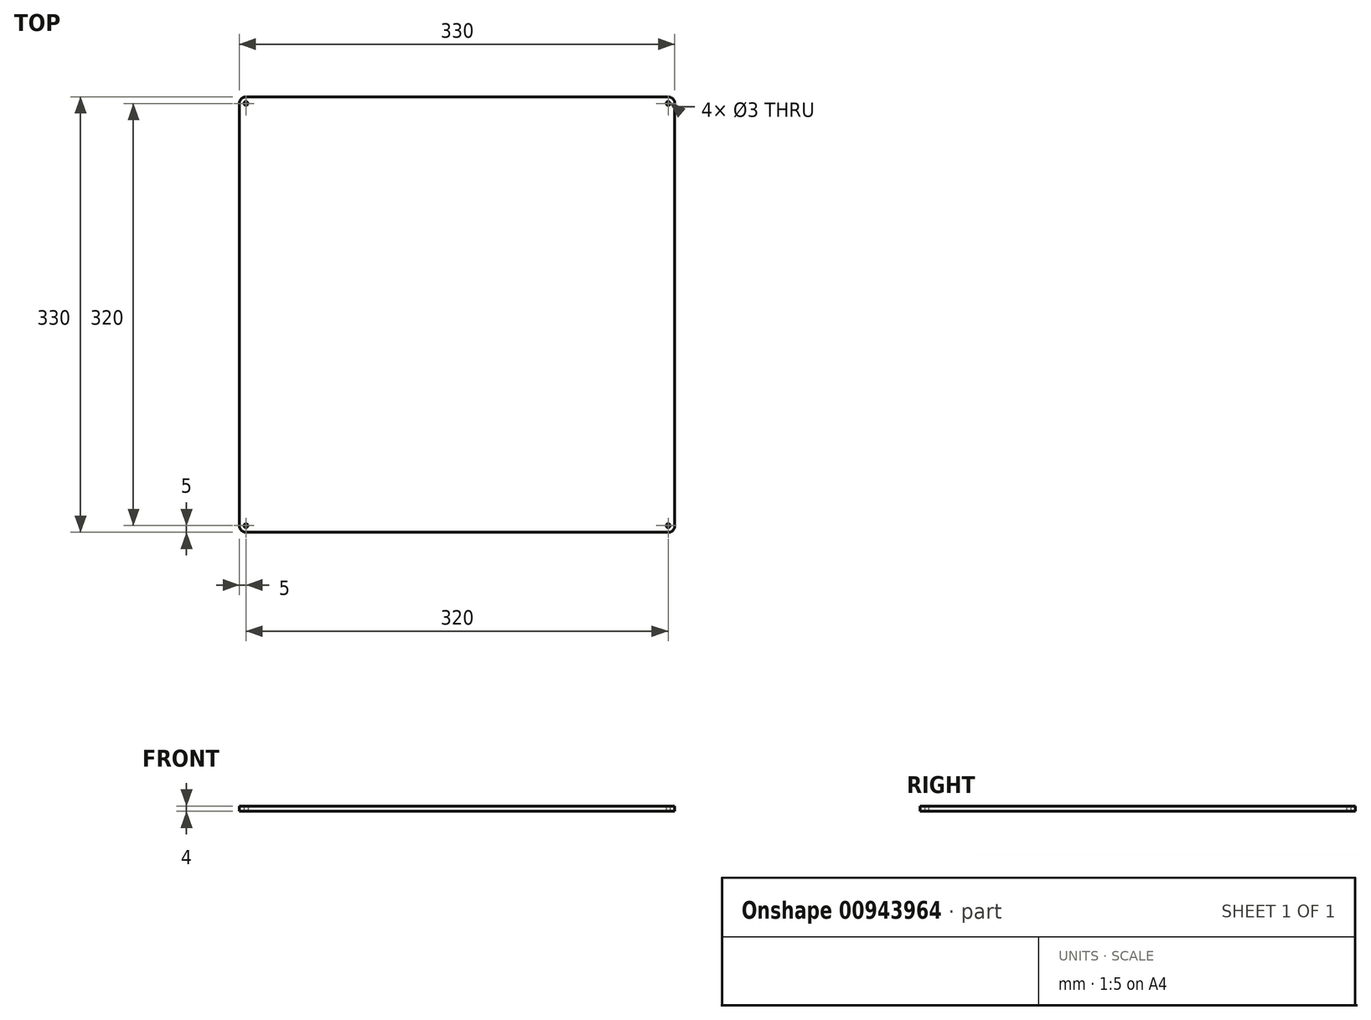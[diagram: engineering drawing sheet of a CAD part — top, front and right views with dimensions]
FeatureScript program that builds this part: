
annotation { "Feature Type Name" : "Feature", "Feature Type Description" : "" }
export const myFeature = defineFeature(function(context is Context, id is Id, definition is map)
    precondition{}
    {
        {
            var Q0;
            Q0=qCreatedBy(makeId("Top.planeOp"),FACE);
            var sketch = newSketch(context, id + "F0", { "sketchPlane" : qUnion([Q0])});
            skLineSegment(sketch, "E0.bottom", {"start": v(165, -165) * mm, "end": v(-165, -165) * mm});
            skLineSegment(sketch, "E0.top", {"start": v(165, 165) * mm, "end": v(-165, 165) * mm});
            skLineSegment(sketch, "E0.left", {"start": v(165, -165) * mm, "end": v(165, 165) * mm});
            skLineSegment(sketch, "E0.right", {"start": v(-165, -165) * mm, "end": v(-165, 165) * mm});
            skPoint(sketch, "E0.middle", {"position": v(0, 0) * mm});
            skCircle(sketch, "E1", {"center": v(-160, 160) * mm, "radius": 1.5 * mm});
            skCircle(sketch, "E2", {"center": v(160, 160) * mm, "radius": 1.5 * mm});
            skCircle(sketch, "E3", {"center": v(160, -160) * mm, "radius": 1.5 * mm});
            skCircle(sketch, "E4", {"center": v(-160, -160) * mm, "radius": 1.5 * mm});
            skSolve(sketch);
        }
        {
            var Q0;
            Q0=makeQuery(id+"F0.imprint","IMPRINT",FACE,{"disambiguationData":[TD([[makeQuery(id+"F0.imprint","IMPRINT",EDGE,{"derivedFrom":sQuery(id+"F0.wireOp",EDGE,"E0.bottom")}),-1.0]])]});
            extrude(context, id + "F1", {"entities" : qUnion([Q0]), "depth" : 4 * mm, "offsetDistance" : 25 * mm});
        }
        {
            var Q0;
            Q0=makeQuery(id+"F1.opExtrude","SWEPT_EDGE",EDGE,{"disambiguationData":[OSD([sQuery(id+"F0.wireOp",EDGE,"E0.bottom"),sQuery(id+"F0.wireOp",EDGE,"E0.left")])]});
            var Q1;
            Q1=makeQuery(id+"F1.opExtrude","SWEPT_EDGE",EDGE,{"disambiguationData":[OSD([sQuery(id+"F0.wireOp",EDGE,"E0.bottom"),sQuery(id+"F0.wireOp",EDGE,"E0.right")])]});
            var Q2;
            Q2=makeQuery(id+"F1.opExtrude","SWEPT_EDGE",EDGE,{"disambiguationData":[OSD([sQuery(id+"F0.wireOp",EDGE,"E0.top"),sQuery(id+"F0.wireOp",EDGE,"E0.right")])]});
            var Q3;
            Q3=makeQuery(id+"F1.opExtrude","SWEPT_EDGE",EDGE,{"disambiguationData":[OSD([sQuery(id+"F0.wireOp",EDGE,"E0.top"),sQuery(id+"F0.wireOp",EDGE,"E0.left")])]});
            fillet(context, id + "F2", {"entities" : qUnion([Q0, Q1, Q2, Q3]), "radius" : 5 * mm, "tangentPropagation" : true, "allowEdgeOverflow" : false});
        }
    });
